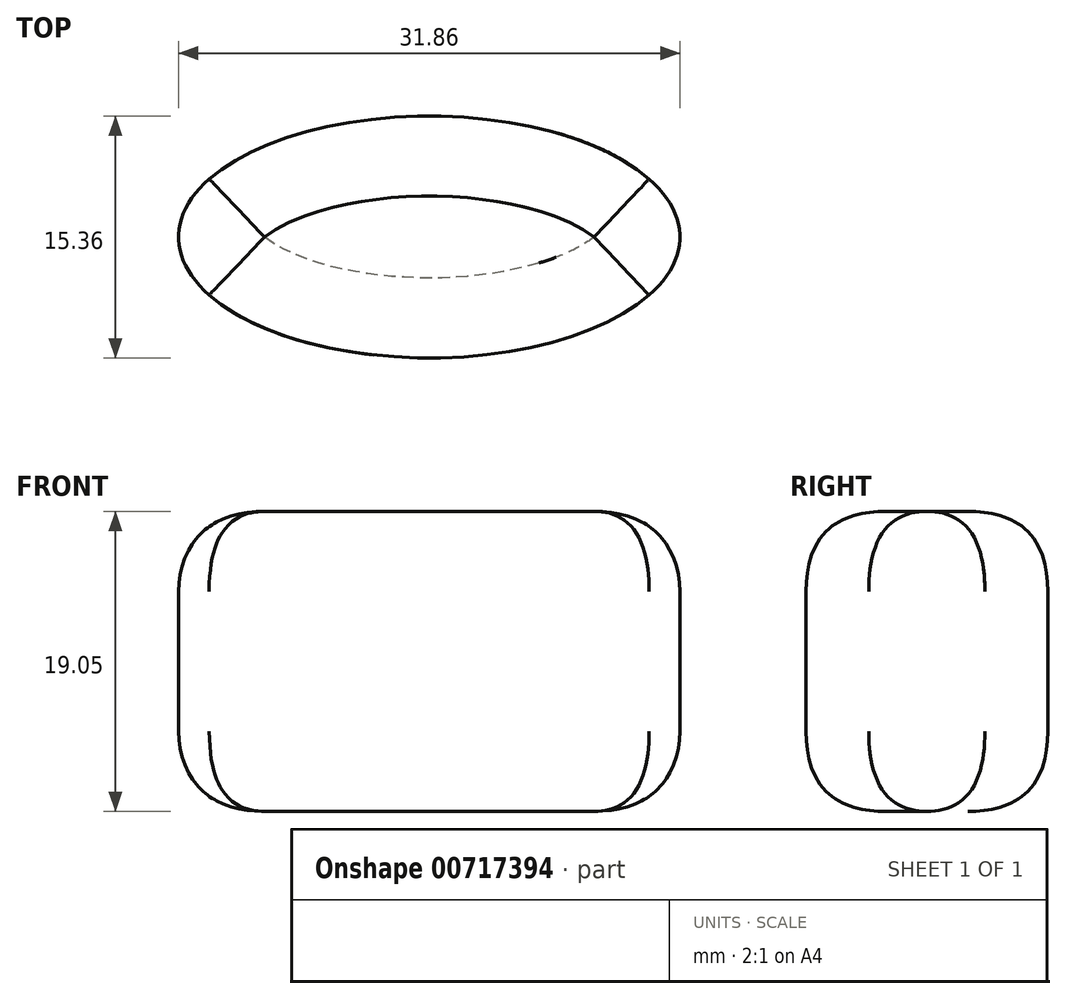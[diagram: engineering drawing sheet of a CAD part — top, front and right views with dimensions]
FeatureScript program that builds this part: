
annotation { "Feature Type Name" : "Feature", "Feature Type Description" : "" }
export const myFeature = defineFeature(function(context is Context, id is Id, definition is map)
    precondition{}
    {
        {
            var Q0;
            Q0=qCreatedBy(makeId("Top.planeOp"),FACE);
            var sketch = newSketch(context, id + "F0", { "sketchPlane" : qUnion([Q0])});
            skLineSegment(sketch, "E0.bottom", {"start": v(-51.17, -48.25) * mm, "end": v(51.74, -48.25) * mm});
            skLineSegment(sketch, "E0.top", {"start": v(-51.17, 48.63) * mm, "end": v(51.74, 48.63) * mm});
            skLineSegment(sketch, "E0.left", {"start": v(-51.17, -48.25) * mm, "end": v(-51.17, 48.63) * mm});
            skLineSegment(sketch, "E0.right", {"start": v(51.74, -48.25) * mm, "end": v(51.74, 48.63) * mm});
            skLineSegment(sketch, "E1.bottom", {"start": v(33.27, 29.21) * mm, "end": v(-34.77, 29.21) * mm});
            skLineSegment(sketch, "E1.top", {"start": v(33.27, -29.97) * mm, "end": v(-34.77, -29.97) * mm});
            skLineSegment(sketch, "E1.left", {"start": v(33.27, 29.21) * mm, "end": v(33.27, -29.97) * mm});
            skLineSegment(sketch, "E1.right", {"start": v(-34.77, 29.21) * mm, "end": v(-34.77, -29.97) * mm});
            skLineSegment(sketch, "E2", {"start": v(38.73, 48.63) * mm, "end": v(38.73, 44.67) * mm});
            skLineSegment(sketch, "E3", {"start": v(38.73, 44.67) * mm, "end": v(47.6, 44.67) * mm});
            skLineSegment(sketch, "E4", {"start": v(47.6, 44.67) * mm, "end": v(47.6, 35.25) * mm});
            skLineSegment(sketch, "E5", {"start": v(47.6, 35.25) * mm, "end": v(51.74, 35.25) * mm});
            skLineSegment(sketch, "E6", {"start": v(-38.54, 48.63) * mm, "end": v(-38.54, 44.3) * mm});
            skLineSegment(sketch, "E7", {"start": v(-38.54, 44.3) * mm, "end": v(-47.21, 44.3) * mm});
            skLineSegment(sketch, "E8", {"start": v(-47.21, 44.3) * mm, "end": v(-47.21, 35.25) * mm});
            skLineSegment(sketch, "E9", {"start": v(-47.21, 35.25) * mm, "end": v(-51.17, 35.25) * mm});
            skEllipse(sketch, "E10", {"center": v(0, 0) * mm, "majorRadius": 15.93 * mm, "minorRadius": 7.68 * mm, "majorAxis": v(-1, 0)});
            skSolve(sketch);
        }
        {
            var Q0;
            Q0=makeQuery(id+"F0.imprint","IMPRINT",FACE,{"disambiguationData":[TD([[makeQuery(id+"F0.imprint","IMPRINT",EDGE,{"derivedFrom":sQuery(id+"F0.wireOp",EDGE,"E10")}),1.0]])]});
            extrude(context, id + "F1", {"entities" : qUnion([Q0]), "oppositeDirection" : true, "depth" : 19.05 * mm, "offsetDistance" : 25.4 * mm});
        }
        {
            var Q0;
            Q0=makeQuery(id+"F1.opExtrude","SWEPT_FACE",FACE,{"disambiguationData":[OSD([sQuery(id+"F0.wireOp",EDGE,"E10")])]});
            fillet(context, id + "F2", {"entities" : qUnion([Q0]), "radius" : 5.08 * mm, "rho" : 0.5, "crossSection" : FilletCrossSection.CONIC, "allowEdgeOverflow" : false});
        }
    });
